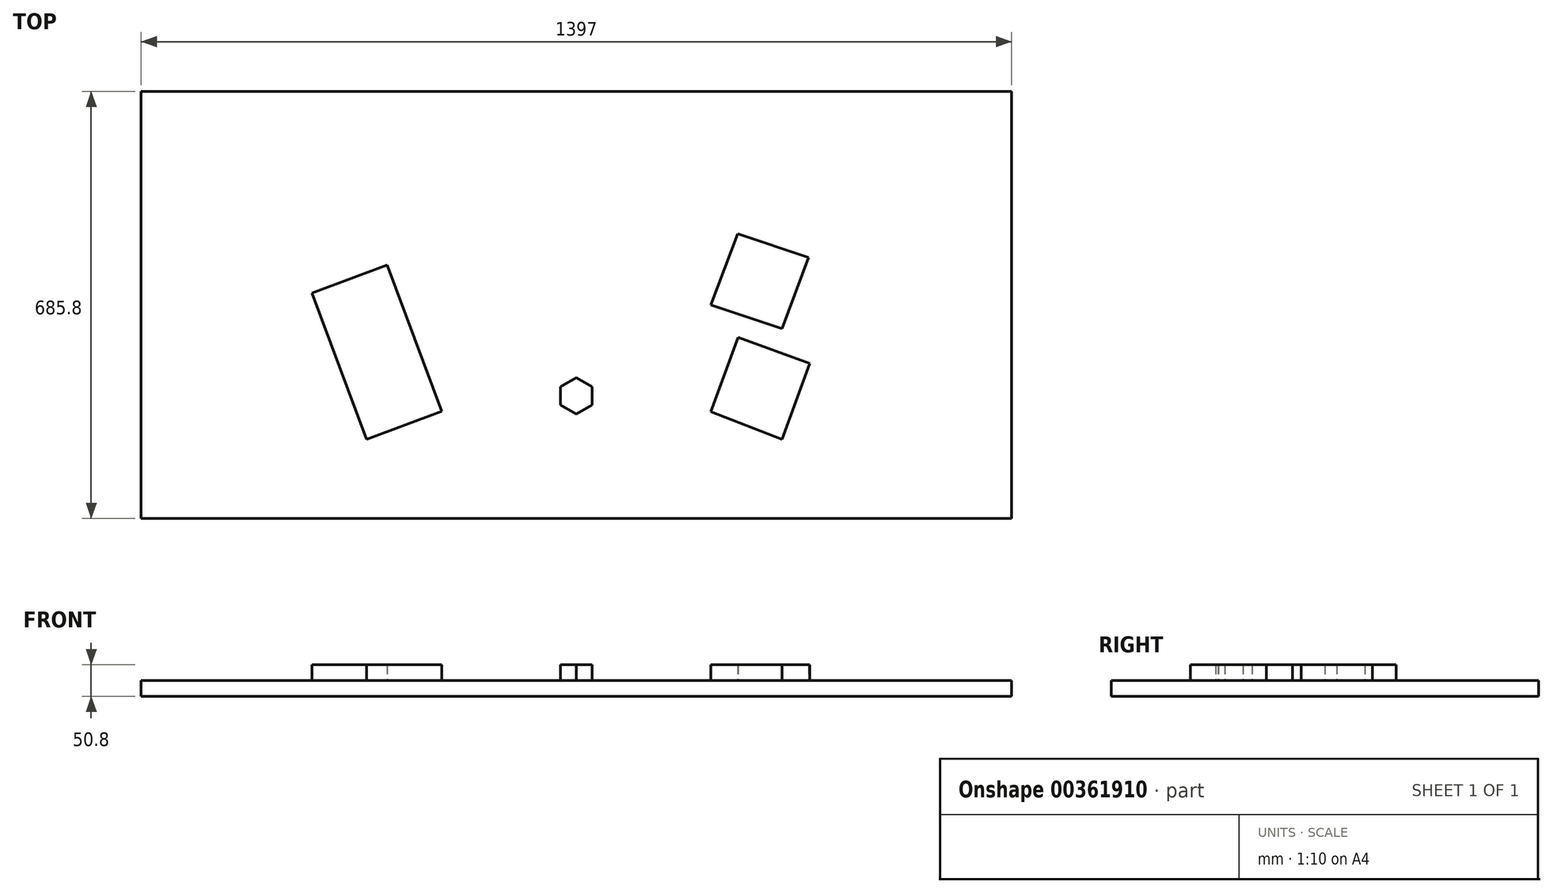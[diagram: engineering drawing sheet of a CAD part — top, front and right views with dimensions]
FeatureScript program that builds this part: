
annotation { "Feature Type Name" : "Feature", "Feature Type Description" : "" }
export const myFeature = defineFeature(function(context is Context, id is Id, definition is map)
    precondition{}
    {
        {
            var Q0;
            Q0=qCreatedBy(makeId("Top.planeOp"),FACE);
            var sketch = newSketch(context, id + "F0", { "sketchPlane" : qUnion([Q0])});
            skLineSegment(sketch, "E0.bottom", {"start": v(698.5, 342.9) * mm, "end": v(-698.5, 342.9) * mm});
            skLineSegment(sketch, "E0.top", {"start": v(698.5, -342.9) * mm, "end": v(-698.5, -342.9) * mm});
            skLineSegment(sketch, "E0.left", {"start": v(698.5, 342.9) * mm, "end": v(698.5, -342.9) * mm});
            skLineSegment(sketch, "E0.right", {"start": v(-698.5, 342.9) * mm, "end": v(-698.5, -342.9) * mm});
            skPoint(sketch, "E0.middle", {"position": v(0, 0) * mm});
            skSolve(sketch);
        }
        {
            var Q0;
            Q0 = qSketchRegion(id + "F0", true);
            extrude(context, id + "F1", {"entities" : qUnion([Q0]), "depth" : 25.4 * mm});
        }
        {
            var Q0;
            Q0=makeQuery(id+"F1.opExtrude","CAP_FACE",FACE,{"disambiguationData":[OSD([sQuery(id+"F0.wireOp",EDGE,"E0.bottom"),sQuery(id+"F0.wireOp",EDGE,"E0.top"),sQuery(id+"F0.wireOp",EDGE,"E0.left"),sQuery(id+"F0.wireOp",EDGE,"E0.right")])],"isStart":false});
            var sketch = newSketch(context, id + "F2", { "sketchPlane" : qUnion([Q0])});
            skLineSegment(sketch, "E1.bottom", {"start": v(190.5, -216.06) * mm, "end": v(-190.5, -216.06) * mm, "construction": true});
            skLineSegment(sketch, "E1.top", {"start": v(190.5, 101.6) * mm, "end": v(-190.5, 101.6) * mm, "construction": true});
            skLineSegment(sketch, "E1.left", {"start": v(190.5, -216.06) * mm, "end": v(190.5, 101.6) * mm, "construction": true});
            skLineSegment(sketch, "E1.right", {"start": v(-190.5, -216.06) * mm, "end": v(-190.5, 101.6) * mm, "construction": true});
            skPoint(sketch, "E1.middle", {"position": v(0, -57.23) * mm});
            skLineSegment(sketch, "E2.bottom", {"start": v(-215.9, -170.86) * mm, "end": v(-336.55, -216.06) * mm});
            skLineSegment(sketch, "E2.top", {"start": v(-303.99, 64.25) * mm, "end": v(-424.64, 19.05) * mm});
            skLineSegment(sketch, "E2.left", {"start": v(-215.9, -170.86) * mm, "end": v(-303.99, 64.25) * mm});
            skLineSegment(sketch, "E2.right", {"start": v(-336.55, -216.06) * mm, "end": v(-424.64, 19.05) * mm});
            skPoint(sketch, "E2.middle", {"position": v(-320.27, -75.9) * mm});
            skPoint(sketch, "E3.endSnap0", {"position": v(0, -342.9) * mm});
            skLineSegment(sketch, "E4.MirrorCS", {"start": v(215.9, -171.45) * mm, "end": v(259.34, -52.1) * mm});
            skLineSegment(sketch, "E5.MirrorCS", {"start": v(330.2, -215.9) * mm, "end": v(374.55, -94.04) * mm});
            skLineSegment(sketch, "E6.MirrorCS", {"start": v(215.9, -171.45) * mm, "end": v(330.2, -215.9) * mm});
            skLineSegment(sketch, "E7", {"start": v(259.34, -52.1) * mm, "end": v(374.55, -94.04) * mm});
            skPoint(sketch, "E8", {"position": v(294.98, -134.04) * mm});
            skCircle(sketch, "E9.cCircle", {"center": v(0, -146.18) * mm, "radius": 25.4 * mm, "construction": true});
            skLineSegment(sketch, "E9.0", {"start": v(-25.4, -160.84) * mm, "end": v(-25.4, -131.51) * mm});
            skLineSegment(sketch, "E9.1", {"start": v(-25.4, -131.51) * mm, "end": v(0, -116.85) * mm});
            skLineSegment(sketch, "E9.2", {"start": v(0, -116.85) * mm, "end": v(25.4, -131.51) * mm});
            skLineSegment(sketch, "E9.3", {"start": v(25.4, -131.51) * mm, "end": v(25.4, -160.84) * mm});
            skLineSegment(sketch, "E9.4", {"start": v(25.4, -160.84) * mm, "end": v(0, -175.5) * mm});
            skLineSegment(sketch, "E9.5", {"start": v(0, -175.5) * mm, "end": v(-25.4, -160.84) * mm});
            skPoint(sketch, "E9.0.midPoint", {"position": v(-25.4, -146.18) * mm});
            skLineSegment(sketch, "E10.MirrorCS", {"start": v(215.9, 0) * mm, "end": v(258.71, 114.3) * mm});
            skLineSegment(sketch, "E11.MirrorCS", {"start": v(330.2, -38.1) * mm, "end": v(372.51, 76.2) * mm});
            skLineSegment(sketch, "E12.MirrorCS", {"start": v(215.9, 0) * mm, "end": v(330.2, -38.1) * mm});
            skLineSegment(sketch, "E13", {"start": v(258.71, 114.3) * mm, "end": v(372.51, 76.2) * mm});
            skPoint(sketch, "E14", {"position": v(296.36, 37.52) * mm});
            skSolve(sketch);
        }
        {
            var Q0;
            Q0 = qSketchRegion(id + "F2", true);
            extrude(context, id + "F3", {"entities" : qUnion([Q0]), "depth" : 25.4 * mm});
        }
    });
